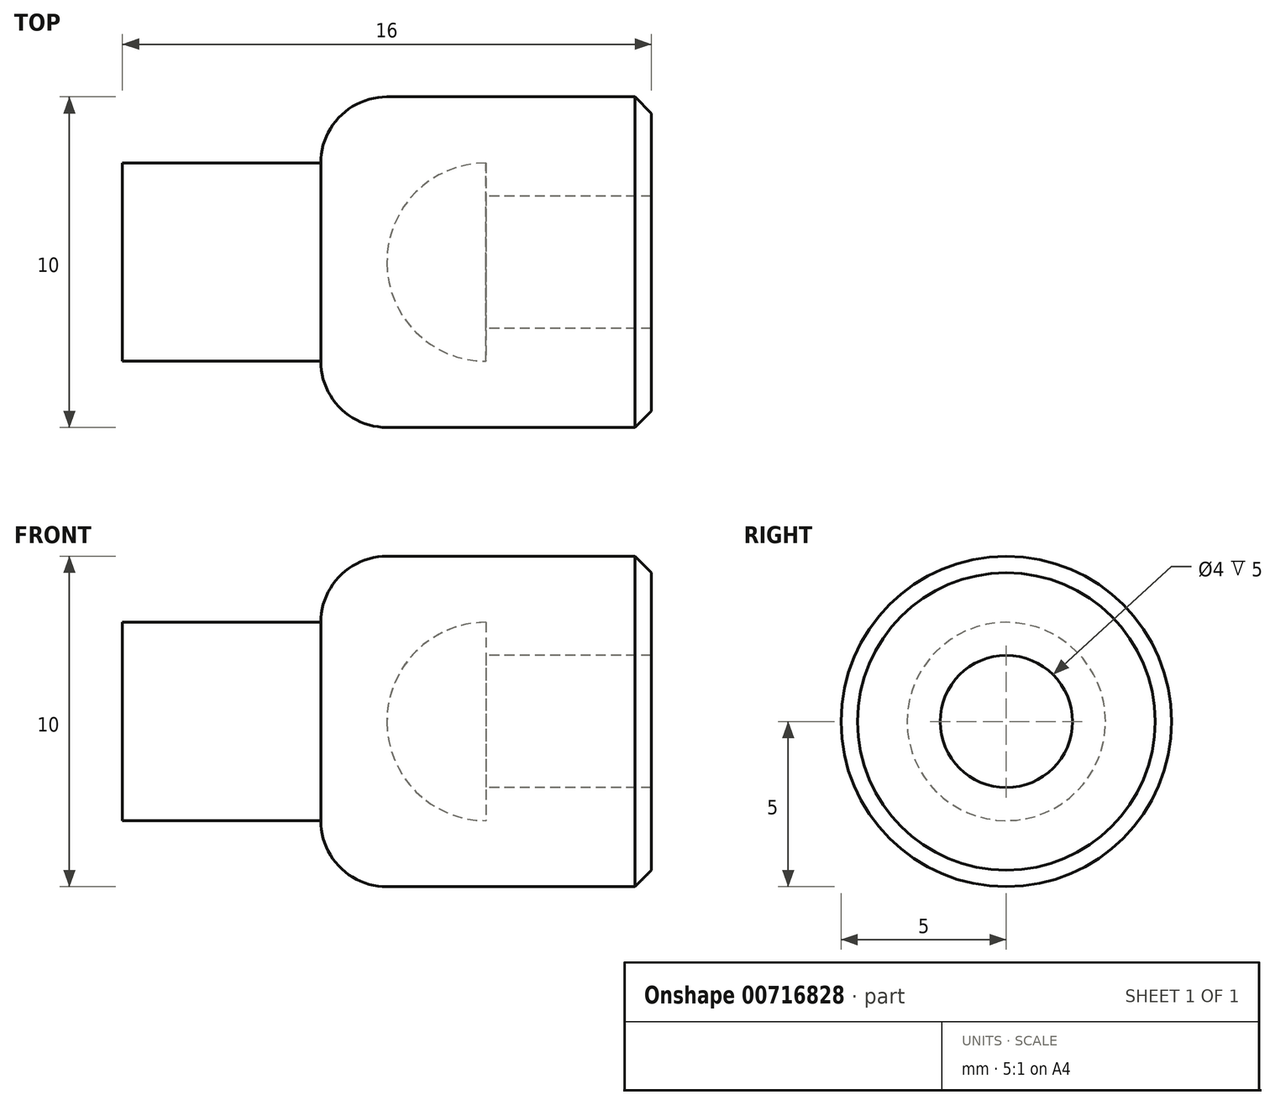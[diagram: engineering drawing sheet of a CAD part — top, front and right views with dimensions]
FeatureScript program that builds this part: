
annotation { "Feature Type Name" : "Feature", "Feature Type Description" : "" }
export const myFeature = defineFeature(function(context is Context, id is Id, definition is map)
    precondition{}
    {
        {
            var Q0;
            Q0=qCreatedBy(makeId("Front.planeOp"),FACE);
            var sketch = newSketch(context, id + "F0", { "sketchPlane" : qUnion([Q0])});
            skLineSegment(sketch, "E0", {"start": v(2, 5) * mm, "end": v(10, 5) * mm});
            skLineSegment(sketch, "E1", {"start": v(2, 0) * mm, "end": v(2, 0) * mm});
            skLineSegment(sketch, "E2", {"start": v(5, 3) * mm, "end": v(5, 3) * mm});
            skLineSegment(sketch, "E3", {"start": v(5, 3) * mm, "end": v(5, 2) * mm});
            skLineSegment(sketch, "E4", {"start": v(5, 2) * mm, "end": v(10, 2) * mm});
            skLineSegment(sketch, "E5", {"start": v(10, 5) * mm, "end": v(10, 2) * mm});
            skLineSegment(sketch, "E6", {"start": v(2, 0) * mm, "end": v(0, 0) * mm});
            skPoint(sketch, "E7.visualSharp", {"position": v(2, 3) * mm});
            skArc(sketch, "E7.filletArc", {"start": v(5, 3) * mm, "mid": v(2.88, 2.12) * mm, "end": v(2, 0) * mm});
            skLineSegment(sketch, "E8", {"start": v(0, 0) * mm, "end": v(12.8, 0) * mm, "construction": true});
            skLineSegment(sketch, "E9", {"start": v(0, 3) * mm, "end": v(-6, 3) * mm});
            skLineSegment(sketch, "E10", {"start": v(-6, 3) * mm, "end": v(-6, 0) * mm});
            skLineSegment(sketch, "E11", {"start": v(-6, 0) * mm, "end": v(0, 0) * mm});
            skPoint(sketch, "E12.visualSharp", {"position": v(0, 5) * mm});
            skArc(sketch, "E12.filletArc", {"start": v(2, 5) * mm, "mid": v(0.59, 4.41) * mm, "end": v(0, 3) * mm});
            skSolve(sketch);
        }
        {
            var Q0;
            Q0=makeQuery(id+"F0.imprint","IMPRINT",FACE,{"disambiguationData":[TD([[makeQuery(id+"F0.imprint","IMPRINT",EDGE,{"derivedFrom":sQuery(id+"F0.wireOp",EDGE,"E0")}),-1.0]])]});
            var Q1;
            Q1=sQuery(id+"F0.wireOp",EDGE,"E8");
            revolve(context, id + "F1", {"surfaceOperationType" : NewSurfaceOperationType.NEW, "entities" : qUnion([Q0]), "axis" : qUnion([Q1]), "revolveType" : RevolveType.FULL});
        }
        {
            var Q0;
            Q0=makeQuery(id+"F1.opRevolve","SWEPT_EDGE",EDGE,{"disambiguationData":[OSD([sQuery(id+"F0.wireOp",EDGE,"E0"),sQuery(id+"F0.wireOp",EDGE,"E5")])]});
            chamfer(context, id + "F2", {"entities" : qUnion([Q0]), "width" : 0.5 * mm, "tangentPropagation" : true});
        }
    });
